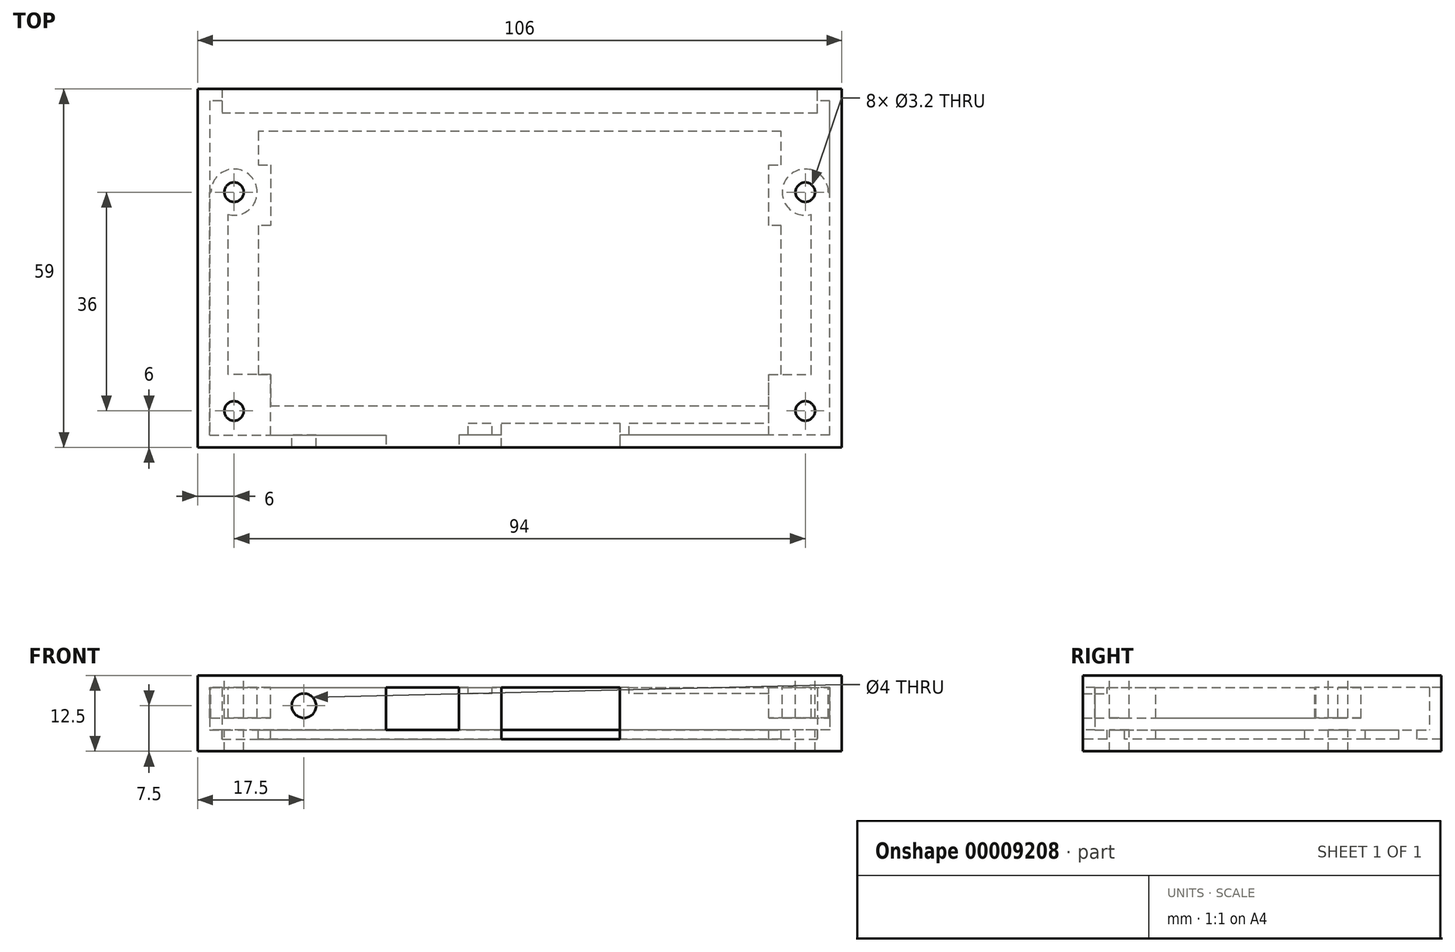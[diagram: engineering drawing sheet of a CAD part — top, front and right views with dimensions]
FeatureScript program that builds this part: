
annotation { "Feature Type Name" : "Feature", "Feature Type Description" : "" }
export const myFeature = defineFeature(function(context is Context, id is Id, definition is map)
    precondition{}
    {
        {
            var Q0;
            Q0=qCreatedBy(makeId("Top.planeOp"),FACE);
            var sketch = newSketch(context, id + "F0", { "sketchPlane" : qUnion([Q0])});
            skLineSegment(sketch, "E0.bottom", {"start": v(-106, 59) * mm, "end": v(0, 59) * mm});
            skLineSegment(sketch, "E0.top", {"start": v(-106, 0) * mm, "end": v(0, 0) * mm});
            skLineSegment(sketch, "E0.left", {"start": v(-106, 59) * mm, "end": v(-106, 0) * mm});
            skLineSegment(sketch, "E0.right", {"start": v(0, 59) * mm, "end": v(0, 0) * mm});
            skSolve(sketch);
        }
        {
            var Q0;
            Q0=makeQuery(id+"F0.imprint","IMPRINT",FACE,{"disambiguationData":[TD([[makeQuery(id+"F0.imprint","IMPRINT",EDGE,{"derivedFrom":sQuery(id+"F0.wireOp",EDGE,"E0.bottom")}),-1.0]])]});
            var sketch = newSketch(context, id + "F1", { "sketchPlane" : qUnion([Q0])});
            skLineSegment(sketch, "E1", {"start": v(-102, 59) * mm, "end": v(-102, 57) * mm});
            skLineSegment(sketch, "E2", {"start": v(-102, 57) * mm, "end": v(-104, 57) * mm});
            skLineSegment(sketch, "E3", {"start": v(-104, 57) * mm, "end": v(-104, 2) * mm});
            skLineSegment(sketch, "E4", {"start": v(-2, 2) * mm, "end": v(-2, 57) * mm});
            skLineSegment(sketch, "E5", {"start": v(-2, 57) * mm, "end": v(-4, 57) * mm});
            skLineSegment(sketch, "E6", {"start": v(-4, 57) * mm, "end": v(-4, 59) * mm});
            skLineSegment(sketch, "E7", {"start": v(-4, 59) * mm, "end": v(0, 59) * mm});
            skLineSegment(sketch, "E8", {"start": v(0, 59) * mm, "end": v(0, 0) * mm});
            skLineSegment(sketch, "E9", {"start": v(0, 0) * mm, "end": v(-106, 0) * mm});
            skLineSegment(sketch, "E10", {"start": v(-106, 0) * mm, "end": v(-106, 59) * mm});
            skLineSegment(sketch, "E11", {"start": v(-106, 59) * mm, "end": v(-102, 59) * mm});
            skLineSegment(sketch, "E12", {"start": v(-104, 2) * mm, "end": v(-75, 2) * mm});
            skLineSegment(sketch, "E13", {"start": v(-75, 2) * mm, "end": v(-75, 0) * mm});
            skLineSegment(sketch, "E14", {"start": v(-75, 0) * mm, "end": v(-106, 0) * mm});
            skLineSegment(sketch, "E15", {"start": v(-63, 2) * mm, "end": v(-63, 0) * mm});
            skLineSegment(sketch, "E16", {"start": v(-63, 0) * mm, "end": v(-56, 0) * mm});
            skLineSegment(sketch, "E17", {"start": v(-56, 0) * mm, "end": v(-56, 2) * mm});
            skLineSegment(sketch, "E18", {"start": v(-56, 2) * mm, "end": v(-63, 2) * mm});
            skLineSegment(sketch, "E19", {"start": v(-2, 2) * mm, "end": v(-36.5, 2) * mm});
            skLineSegment(sketch, "E20", {"start": v(-36.5, 2) * mm, "end": v(-36.5, 0) * mm});
            skLineSegment(sketch, "E21", {"start": v(-36.5, 0) * mm, "end": v(0, 0) * mm});
            skSolve(sketch);
        }
        {
            var Q0;
            Q0 = qSketchRegion(id + "F1", true);
            extrude(context, id + "F2", {"entities" : qUnion([Q0]), "depth" : 7 * mm});
        }
        {
            var Q0;
            Q0 = qSketchRegion(id + "F0", true);
            extrude(context, id + "F3", {"entities" : qUnion([Q0]), "operationType" : NewBodyOperationType.ADD, "oppositeDirection" : true, "depth" : 3.5 * mm});
        }
        {
            var Q0;
            Q0=makeQuery(id+"F2.opExtrude","SWEPT_FACE",FACE,{"disambiguationData":[OSD([sQuery(id+"F1.wireOp",EDGE,"E12")])]});
            var sketch = newSketch(context, id + "F4", { "sketchPlane" : qUnion([Q0])});
            skCircle(sketch, "E22", {"center": v(88.5, 4) * mm, "radius": 2 * mm});
            skSolve(sketch);
        }
        {
            var Q0;
            Q0=makeQuery(id+"F3.opExtrude","CAP_FACE",FACE,{"disambiguationData":[OSD([sQuery(id+"F0.wireOp",EDGE,"E0.bottom"),sQuery(id+"F0.wireOp",EDGE,"E0.top"),sQuery(id+"F0.wireOp",EDGE,"E0.left"),sQuery(id+"F0.wireOp",EDGE,"E0.right")])],"isStart":true});
            var sketch = newSketch(context, id + "F5", { "sketchPlane" : qUnion([Q0])});
            skLineSegment(sketch, "E23", {"start": v(-96, 52) * mm, "end": v(-96, 46.5) * mm});
            skLineSegment(sketch, "E24", {"start": v(-96, 46.5) * mm, "end": v(-94, 46.5) * mm});
            skLineSegment(sketch, "E25", {"start": v(-94, 46.5) * mm, "end": v(-94, 36.5) * mm});
            skLineSegment(sketch, "E26", {"start": v(-94, 36.5) * mm, "end": v(-96, 36.5) * mm});
            skLineSegment(sketch, "E27", {"start": v(-96, 36.5) * mm, "end": v(-96, 12) * mm});
            skLineSegment(sketch, "E28", {"start": v(-96, 12) * mm, "end": v(-94, 12) * mm});
            skLineSegment(sketch, "E29", {"start": v(-94, 12) * mm, "end": v(-94, 6.87) * mm});
            skLineSegment(sketch, "E30", {"start": v(-94, 6.87) * mm, "end": v(-12, 6.87) * mm});
            skLineSegment(sketch, "E31", {"start": v(-12, 6.87) * mm, "end": v(-12, 12) * mm});
            skLineSegment(sketch, "E32", {"start": v(-12, 12) * mm, "end": v(-10, 12) * mm});
            skLineSegment(sketch, "E33", {"start": v(-10, 12) * mm, "end": v(-10, 36.5) * mm});
            skLineSegment(sketch, "E34", {"start": v(-10, 36.5) * mm, "end": v(-12, 36.5) * mm});
            skLineSegment(sketch, "E35", {"start": v(-12, 36.5) * mm, "end": v(-12, 46.5) * mm});
            skLineSegment(sketch, "E36", {"start": v(-12, 46.5) * mm, "end": v(-10, 46.5) * mm});
            skLineSegment(sketch, "E37", {"start": v(-10, 46.5) * mm, "end": v(-10, 52) * mm});
            skLineSegment(sketch, "E38", {"start": v(-10, 52) * mm, "end": v(-96, 52) * mm});
            skPoint(sketch, "E39", {"position": v(-94, 41.5) * mm});
            skLineSegment(sketch, "E40.bottom", {"start": v(-4, 55) * mm, "end": v(-102, 55) * mm});
            skLineSegment(sketch, "E40.top", {"start": v(-4, 59) * mm, "end": v(-102, 59) * mm});
            skLineSegment(sketch, "E40.left", {"start": v(-4, 55) * mm, "end": v(-4, 59) * mm});
            skLineSegment(sketch, "E40.right", {"start": v(-102, 55) * mm, "end": v(-102, 59) * mm});
            skLineSegment(sketch, "E41.bottom", {"start": v(-56, 0) * mm, "end": v(-36.5, 0) * mm});
            skLineSegment(sketch, "E41.top", {"start": v(-56, 4) * mm, "end": v(-36.5, 4) * mm});
            skLineSegment(sketch, "E41.left", {"start": v(-56, 0) * mm, "end": v(-56, 4) * mm});
            skLineSegment(sketch, "E41.right", {"start": v(-36.5, 0) * mm, "end": v(-36.5, 4) * mm});
            skSolve(sketch);
        }
        {
            var Q0;
            Q0 = qSketchRegion(id + "F5", true);
            extrude(context, id + "F6", {"entities" : qUnion([Q0]), "operationType" : NewBodyOperationType.REMOVE, "oppositeDirection" : true, "depth" : 1.5 * mm});
        }
        {
            var Q0;
            Q0=makeQuery(id+"F3.opExtrude","CAP_FACE",FACE,{"disambiguationData":[OSD([sQuery(id+"F0.wireOp",EDGE,"E0.bottom"),sQuery(id+"F0.wireOp",EDGE,"E0.top"),sQuery(id+"F0.wireOp",EDGE,"E0.left"),sQuery(id+"F0.wireOp",EDGE,"E0.right")])],"isStart":true});
            var sketch = newSketch(context, id + "F7", { "sketchPlane" : qUnion([Q0])});
            skCircle(sketch, "E42", {"center": v(-100, 42) * mm, "radius": 1.6 * mm});
            skCircle(sketch, "E43", {"center": v(-100, 6) * mm, "radius": 1.6 * mm});
            skCircle(sketch, "E44", {"center": v(-6, 6) * mm, "radius": 1.6 * mm});
            skCircle(sketch, "E45", {"center": v(-6, 42) * mm, "radius": 1.6 * mm});
            skSolve(sketch);
        }
        {
            var Q0;
            Q0 = qSketchRegion(id + "F7", true);
            var Q1;
            Q1=makeQuery(id+"F3.opExtrude","CAP_FACE",FACE,{"disambiguationData":[OSD([sQuery(id+"F0.wireOp",EDGE,"E0.bottom"),sQuery(id+"F0.wireOp",EDGE,"E0.top"),sQuery(id+"F0.wireOp",EDGE,"E0.left"),sQuery(id+"F0.wireOp",EDGE,"E0.right")])],"isStart":false});
            extrude(context, id + "F8", {"entities" : qUnion([Q0]), "operationType" : NewBodyOperationType.REMOVE, "endBound" : BoundingType.UP_TO_SURFACE, "oppositeDirection" : true, "endBoundEntityFace" : qUnion([Q1]), "depth" : 25 * mm});
        }
        {
            var Q0;
            Q0 = qSketchRegion(id + "F4", true);
            var Q1;
            Q1=makeQuery(id+"F3.boolean.opBoolean","MERGE",FACE,{"derivedFrom":[makeQuery(id+"F2.opExtrude","SWEPT_FACE",FACE,{"disambiguationData":[OSD([sQuery(id+"F1.wireOp",EDGE,"E14")])]}),makeQuery(id+"F2.opExtrude","SWEPT_FACE",FACE,{"disambiguationData":[OSD([sQuery(id+"F1.wireOp",EDGE,"E16")])]}),makeQuery(id+"F2.opExtrude","SWEPT_FACE",FACE,{"disambiguationData":[OSD([sQuery(id+"F1.wireOp",EDGE,"E21")])]}),makeQuery(id+"F3.opExtrude","SWEPT_FACE",FACE,{"disambiguationData":[OSD([sQuery(id+"F0.wireOp",EDGE,"E0.top")])]})]});
            extrude(context, id + "F9", {"entities" : qUnion([Q0]), "operationType" : NewBodyOperationType.REMOVE, "endBound" : BoundingType.UP_TO_SURFACE, "oppositeDirection" : true, "endBoundEntityFace" : qUnion([Q1]), "depth" : 25 * mm});
        }
        {
            var Q0;
            Q0=makeQuery(id+"F2.opExtrude","CAP_FACE",FACE,{"disambiguationData":[OSD([sQuery(id+"F1.wireOp",EDGE,"E1"),sQuery(id+"F1.wireOp",EDGE,"E2"),sQuery(id+"F1.wireOp",EDGE,"E3"),sQuery(id+"F1.wireOp",EDGE,"E10"),sQuery(id+"F1.wireOp",EDGE,"E11"),sQuery(id+"F1.wireOp",EDGE,"E12"),sQuery(id+"F1.wireOp",EDGE,"E13"),sQuery(id+"F1.wireOp",EDGE,"E14")])],"isStart":false});
            var sketch = newSketch(context, id + "F10", { "sketchPlane" : qUnion([Q0])});
            skLineSegment(sketch, "E46.bottom", {"start": v(-106, 59) * mm, "end": v(0, 59) * mm});
            skLineSegment(sketch, "E46.top", {"start": v(-106, 0) * mm, "end": v(0, 0) * mm});
            skLineSegment(sketch, "E46.left", {"start": v(-106, 59) * mm, "end": v(-106, 0) * mm});
            skLineSegment(sketch, "E46.right", {"start": v(0, 59) * mm, "end": v(0, 0) * mm});
            skSolve(sketch);
        }
        {
            var Q0;
            Q0 = qSketchRegion(id + "F10", true);
            extrude(context, id + "F11", {"entities" : qUnion([Q0]), "depth" : 2 * mm});
        }
        {
            var Q0;
            Q0=makeQuery(id+"F11.opExtrude","CAP_FACE",FACE,{"disambiguationData":[OSD([sQuery(id+"F10.wireOp",EDGE,"E46.bottom"),sQuery(id+"F10.wireOp",EDGE,"E46.top"),sQuery(id+"F10.wireOp",EDGE,"E46.left"),sQuery(id+"F10.wireOp",EDGE,"E46.right")])],"isStart":true});
            var sketch = newSketch(context, id + "F12", { "sketchPlane" : qUnion([Q0])});
            skLineSegment(sketch, "E47.bottom", {"start": v(-104, -2) * mm, "end": v(-94, -2) * mm});
            skLineSegment(sketch, "E47.left", {"start": v(-104, -2) * mm, "end": v(-104, -42) * mm});
            skLineSegment(sketch, "E48.bottom", {"start": v(-2, -2) * mm, "end": v(-12, -2) * mm});
            skLineSegment(sketch, "E48.left", {"start": v(-2, -2) * mm, "end": v(-2, -42) * mm});
            skLineSegment(sketch, "E49", {"start": v(-94, -2) * mm, "end": v(-94, -12) * mm});
            skLineSegment(sketch, "E50", {"start": v(-94, -12) * mm, "end": v(-101, -12) * mm});
            skLineSegment(sketch, "E51", {"start": v(-101, -12) * mm, "end": v(-101, -42) * mm});
            skLineSegment(sketch, "E52", {"start": v(-12, -2) * mm, "end": v(-12, -12) * mm});
            skLineSegment(sketch, "E53", {"start": v(-12, -12) * mm, "end": v(-5, -12) * mm});
            skLineSegment(sketch, "E54", {"start": v(-5, -12) * mm, "end": v(-5, -42) * mm});
            skLineSegment(sketch, "E55", {"start": v(-104, -42) * mm, "end": v(-101, -42) * mm});
            skLineSegment(sketch, "E56", {"start": v(-5, -42) * mm, "end": v(-2, -42) * mm});
            skCircle(sketch, "E57", {"center": v(-100, -42) * mm, "radius": 3.8 * mm});
            skCircle(sketch, "E58", {"center": v(-6, -42) * mm, "radius": 3.8 * mm});
            skSolve(sketch);
        }
        {
            var Q0;
            Q0 = qSketchRegion(id + "F12", true);
            extrude(context, id + "F13", {"entities" : qUnion([Q0]), "operationType" : NewBodyOperationType.ADD, "depth" : 5 * mm});
        }
        {
            var Q0;
            Q0=makeQuery(id+"F11.opExtrude","CAP_FACE",FACE,{"disambiguationData":[OSD([sQuery(id+"F10.wireOp",EDGE,"E46.bottom"),sQuery(id+"F10.wireOp",EDGE,"E46.top"),sQuery(id+"F10.wireOp",EDGE,"E46.left"),sQuery(id+"F10.wireOp",EDGE,"E46.right")])],"isStart":false});
            var sketch = newSketch(context, id + "F14", { "sketchPlane" : qUnion([Q0])});
            skCircle(sketch, "E59", {"center": v(-100, 6) * mm, "radius": 1.6 * mm});
            skCircle(sketch, "E60", {"center": v(-100, 42) * mm, "radius": 1.6 * mm});
            skCircle(sketch, "E61", {"center": v(-6, 6) * mm, "radius": 1.6 * mm});
            skCircle(sketch, "E62", {"center": v(-6, 42) * mm, "radius": 1.6 * mm});
            skSolve(sketch);
        }
        {
            var Q0;
            Q0 = qSketchRegion(id + "F14", true);
            extrude(context, id + "F15", {"entities" : qUnion([Q0]), "operationType" : NewBodyOperationType.REMOVE, "oppositeDirection" : true, "depth" : 25 * mm});
        }
        {
            var Q0;
            Q0=makeQuery(id+"F11.opExtrude","CAP_FACE",FACE,{"disambiguationData":[OSD([sQuery(id+"F10.wireOp",EDGE,"E46.bottom"),sQuery(id+"F10.wireOp",EDGE,"E46.top"),sQuery(id+"F10.wireOp",EDGE,"E46.left"),sQuery(id+"F10.wireOp",EDGE,"E46.right")])],"isStart":true});
            var sketch = newSketch(context, id + "F16", { "sketchPlane" : qUnion([Q0])});
            skLineSegment(sketch, "E63.bottom", {"start": v(-35, -2) * mm, "end": v(-12, -2) * mm});
            skLineSegment(sketch, "E63.top", {"start": v(-35, -4) * mm, "end": v(-12, -4) * mm});
            skLineSegment(sketch, "E63.left", {"start": v(-35, -2) * mm, "end": v(-35, -4) * mm});
            skLineSegment(sketch, "E63.right", {"start": v(-12, -2) * mm, "end": v(-12, -4) * mm});
            skLineSegment(sketch, "E64.bottom", {"start": v(-61.5, -2) * mm, "end": v(-57.5, -2) * mm});
            skLineSegment(sketch, "E64.top", {"start": v(-61.5, -4) * mm, "end": v(-57.5, -4) * mm});
            skLineSegment(sketch, "E64.left", {"start": v(-61.5, -2) * mm, "end": v(-61.5, -4) * mm});
            skLineSegment(sketch, "E64.right", {"start": v(-57.5, -2) * mm, "end": v(-57.5, -4) * mm});
            skSolve(sketch);
        }
        {
            var Q0;
            Q0 = qSketchRegion(id + "F16", true);
            extrude(context, id + "F17", {"entities" : qUnion([Q0]), "operationType" : NewBodyOperationType.ADD, "depth" : 1 * mm});
        }
    });
